# Revit family: SANINDUSA_130022004_ProgetConfort_ProgetConfortWlDclosecoupledtoilet345x685x450_V0
name_source: partatom
category: Plumbing Fixtures
revit_build: Autodesk Revit 2018 (Build: 20170223_1515(x64)
units: mm (PartAtom-declared; Revit-internal decimal feet)

## family parameters
Cut with Voids When Loaded = No
Host = Face
Part Type = Normal
Room Calculation Point = No
Round Connector Dimension = Use Diameter
Shared = No

## types (1)
- SANINDUSA_130022004_ProgetConfort_ProgetConfortWlDclosecoupledtoilet345x685x450_V0
    AssetType = Fixed
    CodePerformance = EN 997:2012  CL 1 - 6 A
    Color = white
    Constituents = Compatible toilet seats (not included): 21411 - Proget Confort toilet seat; ;  Compatible cisterns: 130111LM - Proget Confort bottom water supply connection cistern with dual flush mechanism; 130113LM - Proget Confort side water supply connection cistern with dual flush mechanism; 24 - fixing kit (included).
    Default Elevation = 1219 mm
    Description = Soil appliance for the disposal of excrement.
    DrainSize = 100 mm  [stored 0.328084 ft]
    Element Type = TOILETPAN: Soil appliance for the disposal of excrement.
    Features = Domestic and commercial use. Versatile timeless design. Seats with clipoff system easy to clean and slow close option. Back to wall WC. 
commercial use. Versatile timeless design. Seats with clipoff system easy to clean and slow close option. Back to wall WC."
    Finish = gloss
    InletDiameter = 0 mm  [stored 0 ft]
    Installation Instructions = https://www.tec.sanindusa.pt
    InstallationDate = 1900-12-31T23:59:59
    Manufacturer = Sanindusa
    ManufacturerName = Sanindusa
    ManufacturerURL = www.tec.sanindusa.pt
    Material = vitreous china
    Model = 130022004
    ModelNumber = 130022004
    ModelReference = Proget Confort
    Name = Proget Confort W|D close coupled toilet
    NominalHeight = 450 mm  [stored 1.47638 ft]
    NominalLength = 345 mm  [stored 1.13189 ft]
    NominalWidth = 685 mm
    PanColor = white
    PanMaterial = vitreous china
    Pre-defined type (IFC) = TOILETPAN
    ProductInformation = https://www.tec.sanindusa.pt
    ProductionYear = 2010
    Size = 345x685x450
    ToiletPanType = washdown
    ToiletType = LooseCoupled
    Type (IFC) = IfcSanitaryTerminalType
    URL = www.tec.sanindusa.pt
    Uniclass2015Code = Pr_40_20_93_94
    Uniclass2015Title = WC pans
    Uniclass2015Version = Products v1.6
    Version = 1
    WarrantyDescription = https://www.tec.sanindusa.pt
    WarrantyDurationParts = 5
    WarrantyDurationUnit = year
    WarrantyStartDate = 1900-12-31T23:59:59
    Waste Connection = Yes
    Weight = 26.80 kg

note: [stored X ft] marks values corroborated as IEEE doubles in the binary element streams (Revit-internal decimal feet)

## geometry (parser evidence)
native form markers: Sweep x5
no freeform markers — native parametric forms only
